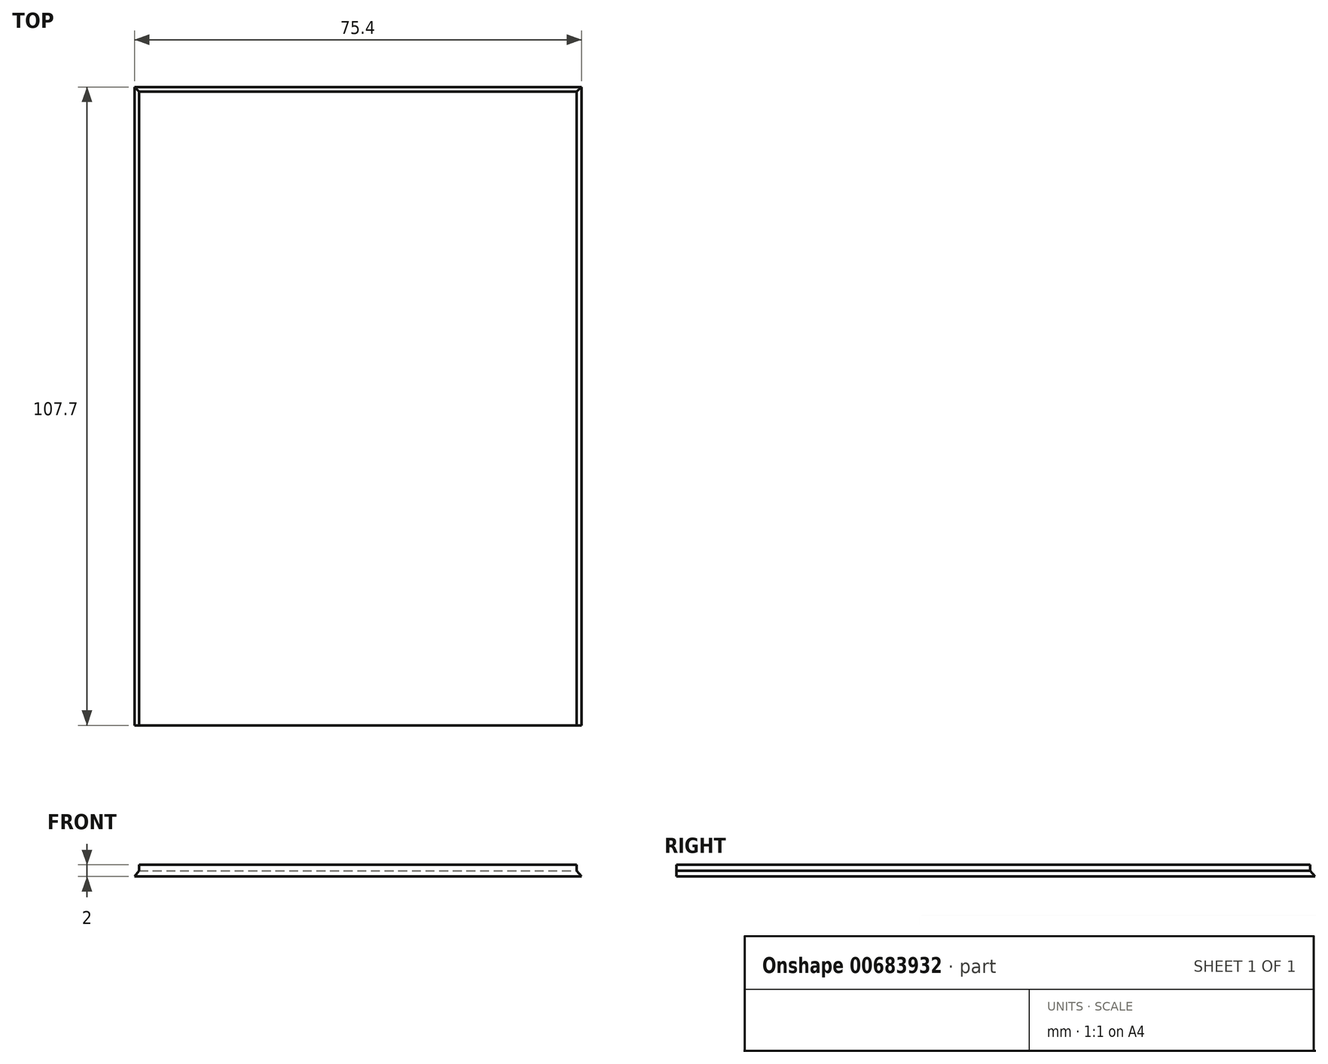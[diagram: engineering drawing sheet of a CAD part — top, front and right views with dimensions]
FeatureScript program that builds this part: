
annotation { "Feature Type Name" : "Feature", "Feature Type Description" : "" }
export const myFeature = defineFeature(function(context is Context, id is Id, definition is map)
    precondition{}
    {
        {
            var Q0;
            Q0=qCreatedBy(makeId("Front.planeOp"),FACE);
            var sketch = newSketch(context, id + "F0", { "sketchPlane" : qUnion([Q0])});
            skLineSegment(sketch, "E0", {"start": v(0.8, 1) * mm, "end": v(0.8, 2) * mm});
            skLineSegment(sketch, "E1", {"start": v(0.8, 2) * mm, "end": v(74.6, 2) * mm});
            skLineSegment(sketch, "E2", {"start": v(74.6, 2) * mm, "end": v(74.6, 1) * mm});
            skLineSegment(sketch, "E3", {"start": v(75.4, 0) * mm, "end": v(0, 0) * mm});
            skLineSegment(sketch, "E4", {"start": v(0, 0) * mm, "end": v(0.8, 1) * mm});
            skLineSegment(sketch, "E5", {"start": v(74.6, 1) * mm, "end": v(75.4, 0) * mm});
            skSolve(sketch);
        }
        {
            var Q0;
            Q0 = qSketchRegion(id + "F0", true);
            extrude(context, id + "F1", {"entities" : qUnion([Q0]), "oppositeDirection" : true, "depth" : 109 * mm, "offsetDistance" : 25 * mm});
        }
        {
            var Q0;
            Q0=makeQuery(id+"F1.opExtrude","SWEPT_FACE",FACE,{"disambiguationData":[OSD([sQuery(id+"F0.wireOp",EDGE,"E2")])]});
            var sketch = newSketch(context, id + "F2", { "sketchPlane" : qUnion([Q0])});
            skLineSegment(sketch, "E6", {"start": v(109, 2) * mm, "end": v(106.9, 2) * mm});
            skLineSegment(sketch, "E7", {"start": v(106.9, 2) * mm, "end": v(106.9, 1) * mm});
            skLineSegment(sketch, "E8", {"start": v(106.9, 1) * mm, "end": v(107.7, 0) * mm});
            skLineSegment(sketch, "E9", {"start": v(107.7, 0) * mm, "end": v(109, 0) * mm});
            skLineSegment(sketch, "E10", {"start": v(109, 0) * mm, "end": v(109, 2) * mm});
            skSolve(sketch);
        }
        {
            var Q0;
            Q0 = qSketchRegion(id + "F2", true);
            extrude(context, id + "F3", {"entities" : qUnion([Q0]), "operationType" : NewBodyOperationType.REMOVE, "endBound" : BoundingType.SYMMETRIC, "oppositeDirection" : true, "depth" : 159.4 * mm, "offsetDistance" : 25 * mm});
        }
    });
